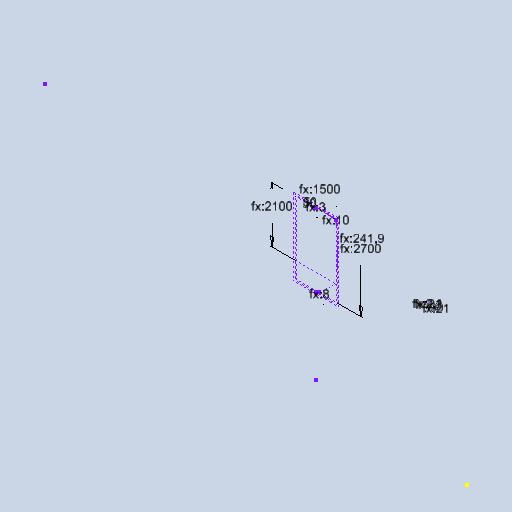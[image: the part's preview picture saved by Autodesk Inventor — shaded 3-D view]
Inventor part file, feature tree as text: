
AUTODESK INVENTOR PART (.ipt)
format: ipt  version: 2025 (Build 290162010, 162A)  size: 122,368 bytes
history: native  units: mm
features: sketch x1
ambient origin geometry x8: Origin, YZ Plane, XZ Plane, XY Plane, X Axis, Y Axis, Z Axis, Center Point
feature tree (1):
  sketch  "Sketch3"  dims[d136=1500.0mm d137=2700.0mm d138=2100.0mm d139=8.0mm d140=50.0mm d141=50.0mm d142=3.0mm d143=10.0mm d144=241.9mm d148=3.0mm d150=5.0mm d194=2.1mm d195=21.0mm d196=21.0mm d197=300.0mm d200=2.0mm d201=30.0mm]
